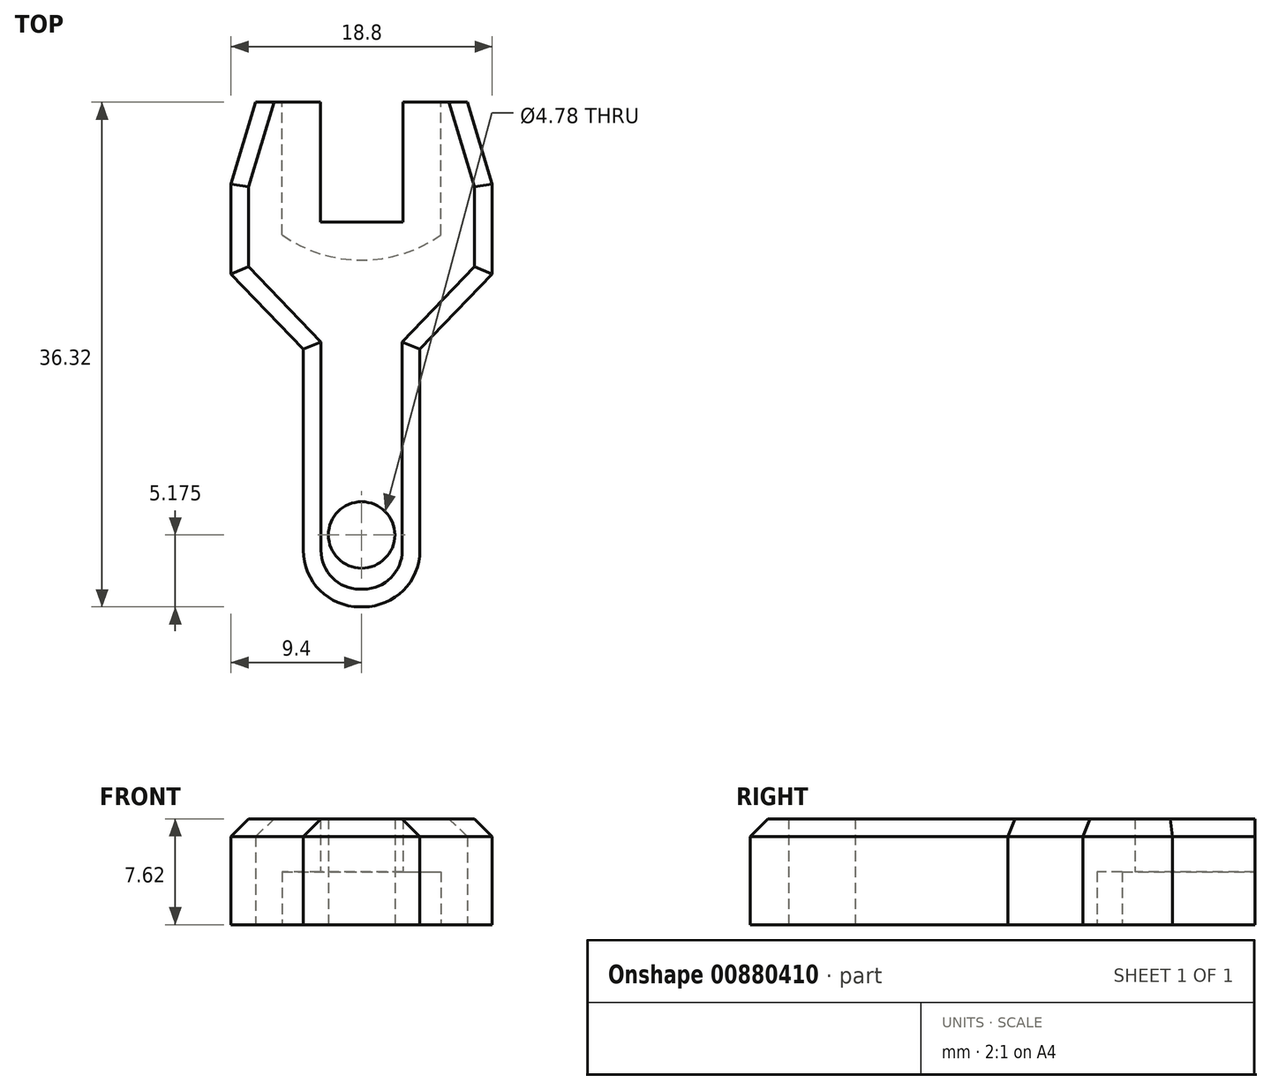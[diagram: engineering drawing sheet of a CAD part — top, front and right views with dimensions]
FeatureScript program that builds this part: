
annotation { "Feature Type Name" : "Feature", "Feature Type Description" : "" }
export const myFeature = defineFeature(function(context is Context, id is Id, definition is map)
    precondition{}
    {
        {
            var Q0;
            Q0=qCreatedBy(makeId("Top.planeOp"),FACE);
            var sketch = newSketch(context, id + "F0", { "sketchPlane" : qUnion([Q0])});
            skLineSegment(sketch, "E0", {"start": v(0, 28.8) * mm, "end": v(0, -27.65) * mm, "construction": true});
            skLineSegment(sketch, "E1", {"start": v(-5.71, 9.8) * mm, "end": v(-5.71, 19.34) * mm});
            skLineSegment(sketch, "E2", {"start": v(-5.71, 19.34) * mm, "end": v(-7.62, 19.34) * mm});
            skLineSegment(sketch, "E3", {"start": v(-7.62, 19.34) * mm, "end": v(-9.4, 13.43) * mm});
            skLineSegment(sketch, "E4", {"start": v(-9.4, 13.43) * mm, "end": v(-9.4, 6.98) * mm});
            skLineSegment(sketch, "E5", {"start": v(-9.4, 6.98) * mm, "end": v(-4.2, 1.57) * mm});
            skLineSegment(sketch, "E6", {"start": v(-4.2, 1.57) * mm, "end": v(-4.2, -12.91) * mm});
            skLineSegment(sketch, "E7", {"start": v(-0.13, -16.98) * mm, "end": v(0, -16.98) * mm});
            skLineSegment(sketch, "E8.MirrorCS", {"start": v(0.13, -16.98) * mm, "end": v(0, -16.98) * mm});
            skLineSegment(sketch, "E9.MirrorCS", {"start": v(4.2, 1.57) * mm, "end": v(4.2, -12.91) * mm});
            skLineSegment(sketch, "E10.MirrorCS", {"start": v(9.4, 6.98) * mm, "end": v(4.2, 1.57) * mm});
            skLineSegment(sketch, "E11.MirrorCS", {"start": v(9.4, 13.43) * mm, "end": v(9.4, 6.98) * mm});
            skLineSegment(sketch, "E12.MirrorCS", {"start": v(7.62, 19.34) * mm, "end": v(9.4, 13.43) * mm});
            skLineSegment(sketch, "E13.MirrorCS", {"start": v(5.71, 19.34) * mm, "end": v(7.62, 19.34) * mm});
            skLineSegment(sketch, "E14.MirrorCS", {"start": v(5.71, 9.8) * mm, "end": v(5.71, 19.34) * mm});
            skArc(sketch, "E15", {"start": v(-5.71, 9.8) * mm, "mid": v(0, 7.98) * mm, "end": v(5.71, 9.8) * mm});
            skPoint(sketch, "E16.start.orphan", {"position": v(0, 11.75) * mm});
            skPoint(sketch, "E17.visualSharp", {"position": v(-4.2, -16.98) * mm});
            skArc(sketch, "E17.filletArc", {"start": v(-4.2, -12.91) * mm, "mid": v(-3, -15.79) * mm, "end": v(-0.13, -16.98) * mm});
            skCircle(sketch, "E18", {"center": v(0, -11.8) * mm, "radius": 2.39 * mm});
            skPoint(sketch, "E19.visualSharp", {"position": v(4.2, -16.98) * mm});
            skArc(sketch, "E19.filletArc", {"start": v(0.13, -16.98) * mm, "mid": v(3, -15.79) * mm, "end": v(4.2, -12.91) * mm});
            skSolve(sketch);
        }
        {
            var Q0;
            Q0=makeQuery(id+"F0.imprint","IMPRINT",FACE,{"disambiguationData":[TD([[makeQuery(id+"F0.imprint","IMPRINT",EDGE,{"derivedFrom":sQuery(id+"F0.wireOp",EDGE,"E1")}),1.0]])]});
            extrude(context, id + "F1", {"entities" : qUnion([Q0]), "depth" : 3.8 * mm, "offsetDistance" : 25.4 * mm});
        }
        {
            var Q0;
            Q0=makeQuery(id+"F1.opExtrude","CAP_FACE",FACE,{"disambiguationData":[OSD([sQuery(id+"F0.wireOp",EDGE,"E1"),sQuery(id+"F0.wireOp",EDGE,"E2"),sQuery(id+"F0.wireOp",EDGE,"E3"),sQuery(id+"F0.wireOp",EDGE,"E4"),sQuery(id+"F0.wireOp",EDGE,"E5"),sQuery(id+"F0.wireOp",EDGE,"E6"),sQuery(id+"F0.wireOp",EDGE,"E7"),sQuery(id+"F0.wireOp",EDGE,"E8.MirrorCS"),sQuery(id+"F0.wireOp",EDGE,"E9.MirrorCS"),sQuery(id+"F0.wireOp",EDGE,"E10.MirrorCS"),sQuery(id+"F0.wireOp",EDGE,"E11.MirrorCS"),sQuery(id+"F0.wireOp",EDGE,"E12.MirrorCS"),sQuery(id+"F0.wireOp",EDGE,"E13.MirrorCS"),sQuery(id+"F0.wireOp",EDGE,"E14.MirrorCS"),sQuery(id+"F0.wireOp",EDGE,"E15"),sQuery(id+"F0.wireOp",EDGE,"E17.filletArc"),sQuery(id+"F0.wireOp",EDGE,"E18"),sQuery(id+"F0.wireOp",EDGE,"E19.filletArc")])],"isStart":false});
            var sketch = newSketch(context, id + "F2", { "sketchPlane" : qUnion([Q0])});
            skLineSegment(sketch, "E20", {"start": v(-5.71, 19.34) * mm, "end": v(-2.97, 19.34) * mm});
            skLineSegment(sketch, "E21", {"start": v(-2.97, 19.34) * mm, "end": v(-2.97, 10.72) * mm});
            skLineSegment(sketch, "E22", {"start": v(-2.97, 10.72) * mm, "end": v(0, 10.72) * mm});
            skLineSegment(sketch, "E23.MirrorCS", {"start": v(2.97, 10.72) * mm, "end": v(0, 10.72) * mm});
            skLineSegment(sketch, "E24.MirrorCS", {"start": v(5.71, 19.34) * mm, "end": v(2.97, 19.34) * mm});
            skLineSegment(sketch, "E25.MirrorCS", {"start": v(2.97, 19.34) * mm, "end": v(2.97, 10.72) * mm});
            skSolve(sketch);
        }
        {
            var Q0;
            Q0=makeQuery(id+"F2.imprint","IMPRINT",FACE,{"disambiguationData":[TD([[makeQuery(id+"F2.imprint","IMPRINT",EDGE,{"derivedFrom":makeQuery(id+"F1.opExtrude","CAP_EDGE",EDGE,{"disambiguationData":[OSD([sQuery(id+"F0.wireOp",EDGE,"E1")])],"isStart":false})}),1.0]])]});
            var Q1;
            Q1=makeQuery(id+"F2.imprint","IMPRINT",FACE,{"disambiguationData":[TD([[makeQuery(id+"F2.imprint","IMPRINT",EDGE,{"derivedFrom":sQuery(id+"F2.wireOp",EDGE,"E20")}),-1.0]])]});
            extrude(context, id + "F3", {"entities" : qUnion([Q0, Q1]), "operationType" : NewBodyOperationType.ADD, "depth" : 3.8 * mm, "offsetDistance" : 25.4 * mm});
        }
        {
            var Q0;
            Q0=makeQuery(id+"F3.opExtrude","CAP_EDGE",EDGE,{"disambiguationData":[OSD([sQuery(id+"F0.wireOp",EDGE,"E3")])],"isStart":false});
            var Q1;
            Q1=makeQuery(id+"F3.opExtrude","CAP_EDGE",EDGE,{"disambiguationData":[OSD([sQuery(id+"F0.wireOp",EDGE,"E4")])],"isStart":false});
            var Q2;
            Q2=makeQuery(id+"F3.opExtrude","CAP_EDGE",EDGE,{"disambiguationData":[OSD([sQuery(id+"F0.wireOp",EDGE,"E5")])],"isStart":false});
            var Q3;
            Q3=makeQuery(id+"F3.opExtrude","CAP_EDGE",EDGE,{"disambiguationData":[OSD([sQuery(id+"F0.wireOp",EDGE,"E6")])],"isStart":false});
            var Q4;
            Q4=makeQuery(id+"F3.opExtrude","CAP_EDGE",EDGE,{"disambiguationData":[OSD([sQuery(id+"F0.wireOp",EDGE,"E10.MirrorCS")])],"isStart":false});
            var Q5;
            Q5=makeQuery(id+"F3.opExtrude","CAP_EDGE",EDGE,{"disambiguationData":[OSD([sQuery(id+"F0.wireOp",EDGE,"E11.MirrorCS")])],"isStart":false});
            var Q6;
            Q6=makeQuery(id+"F3.opExtrude","CAP_EDGE",EDGE,{"disambiguationData":[OSD([sQuery(id+"F0.wireOp",EDGE,"E12.MirrorCS")])],"isStart":false});
            chamfer(context, id + "F4", {"entities" : qUnion([Q0, Q1, Q2, Q3, Q4, Q5, Q6]), "width" : 1.27 * mm, "tangentPropagation" : true});
        }
    });
